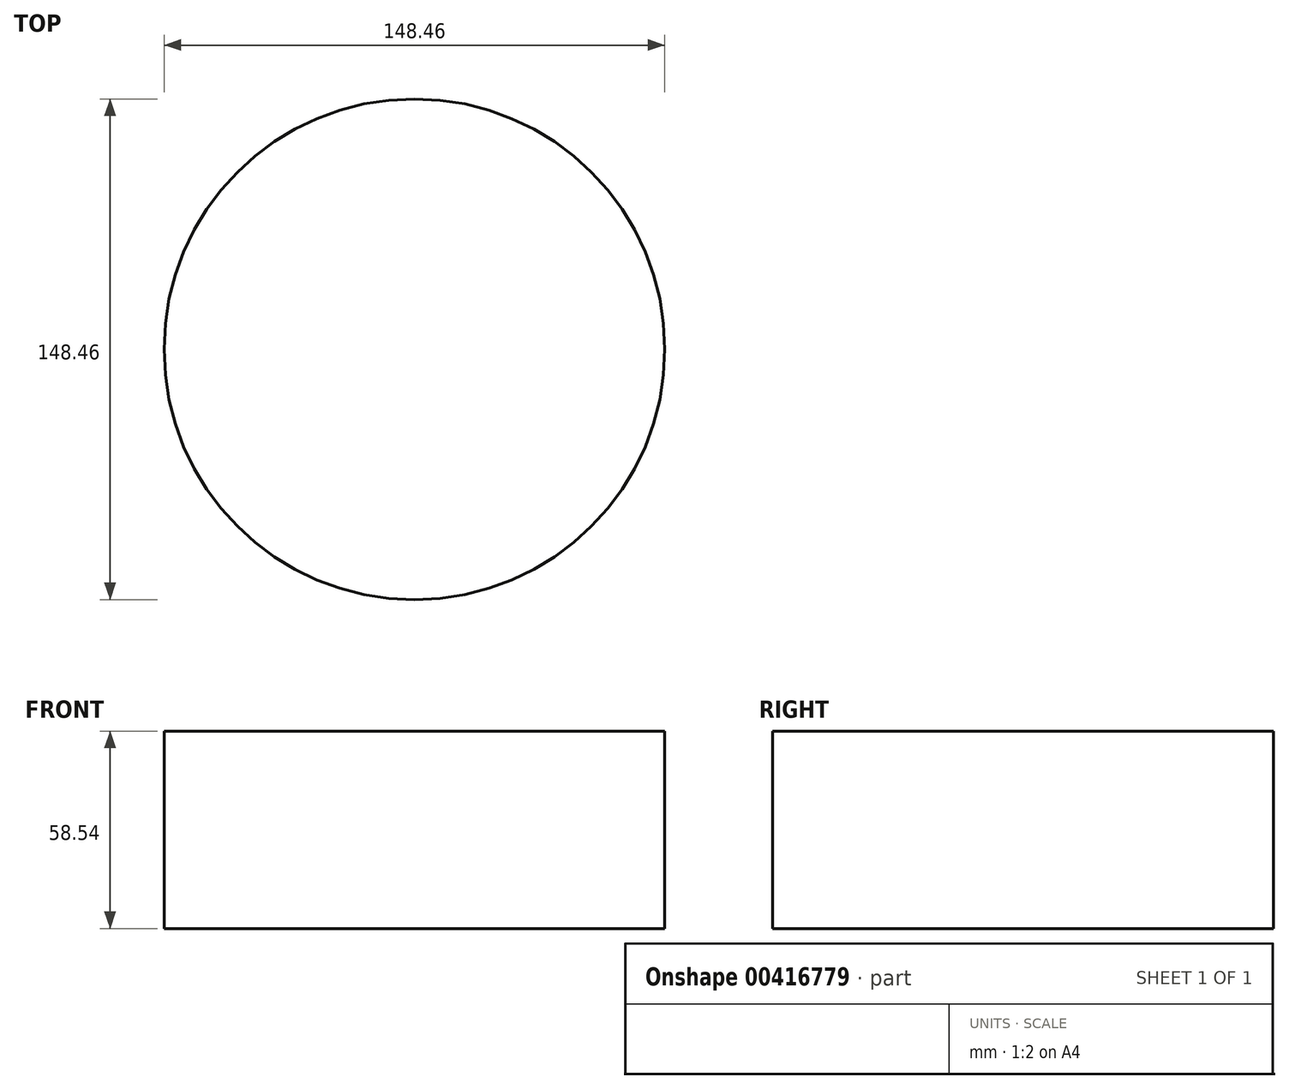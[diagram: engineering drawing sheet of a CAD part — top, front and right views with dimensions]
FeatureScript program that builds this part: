
annotation { "Feature Type Name" : "Feature", "Feature Type Description" : "" }
export const myFeature = defineFeature(function(context is Context, id is Id, definition is map)
    precondition{}
    {
        {
            var Q0;
            Q0=qCreatedBy(makeId("Top.planeOp"),FACE);
            var sketch = newSketch(context, id + "F0", { "sketchPlane" : qUnion([Q0])});
            skCircle(sketch, "E0", {"center": v(0, 0) * mm, "radius": 74.23 * mm});
            skSolve(sketch);
        }
        {
            var Q0;
            Q0 = qSketchRegion(id + "F0", true);
            extrude(context, id + "F1", {"entities" : qUnion([Q0]), "depth" : 58.54 * mm});
        }
    });
